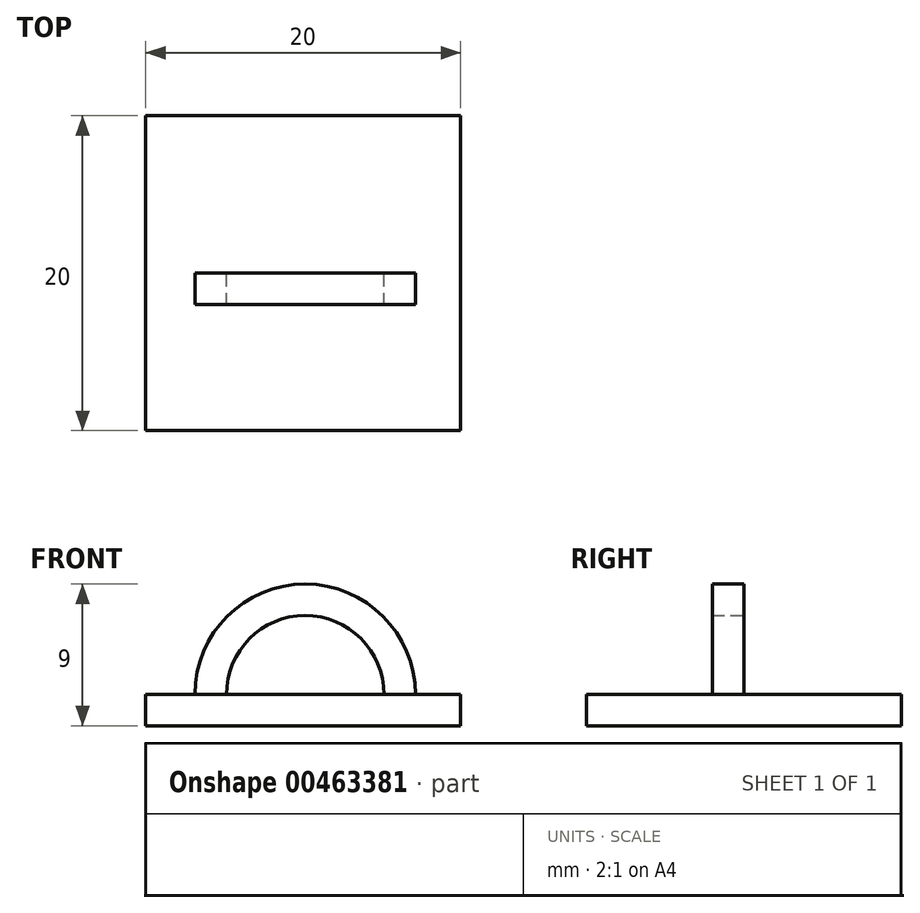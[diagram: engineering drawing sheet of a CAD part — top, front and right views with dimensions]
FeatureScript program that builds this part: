
annotation { "Feature Type Name" : "Feature", "Feature Type Description" : "" }
export const myFeature = defineFeature(function(context is Context, id is Id, definition is map)
    precondition{}
    {
        {
            var Q0;
            Q0=qCreatedBy(makeId("Top.planeOp"),FACE);
            var sketch = newSketch(context, id + "F0", { "sketchPlane" : qUnion([Q0])});
            skLineSegment(sketch, "E0.bottom", {"start": v(-10, 10) * mm, "end": v(10, 10) * mm});
            skLineSegment(sketch, "E0.top", {"start": v(-10, -10) * mm, "end": v(10, -10) * mm});
            skLineSegment(sketch, "E0.left", {"start": v(-10, 10) * mm, "end": v(-10, -10) * mm});
            skLineSegment(sketch, "E0.right", {"start": v(10, 10) * mm, "end": v(10, -10) * mm});
            skSolve(sketch);
        }
        {
            var Q0;
            Q0=qCreatedBy(makeId("Front.planeOp"),FACE);
            var sketch = newSketch(context, id + "F1", { "sketchPlane" : qUnion([Q0])});
            skArc(sketch, "E1", {"start": v(5.13, 2) * mm, "mid": v(0.13, 7) * mm, "end": v(-4.87, 2) * mm});
            skArc(sketch, "E2", {"start": v(7.13, 2) * mm, "mid": v(0.13, 9) * mm, "end": v(-6.87, 2) * mm});
            skLineSegment(sketch, "E3", {"start": v(-6.87, 2) * mm, "end": v(-4.87, 2) * mm});
            skLineSegment(sketch, "E4", {"start": v(5.13, 2) * mm, "end": v(7.13, 2) * mm});
            skSolve(sketch);
        }
        {
            var Q0;
            Q0 = qSketchRegion(id + "F0", true);
            extrude(context, id + "F2", {"entities" : qUnion([Q0]), "depth" : 2 * mm});
        }
        {
            var Q0;
            Q0 = qSketchRegion(id + "F1", true);
            extrude(context, id + "F3", {"entities" : qUnion([Q0]), "depth" : 2 * mm});
        }
    });
